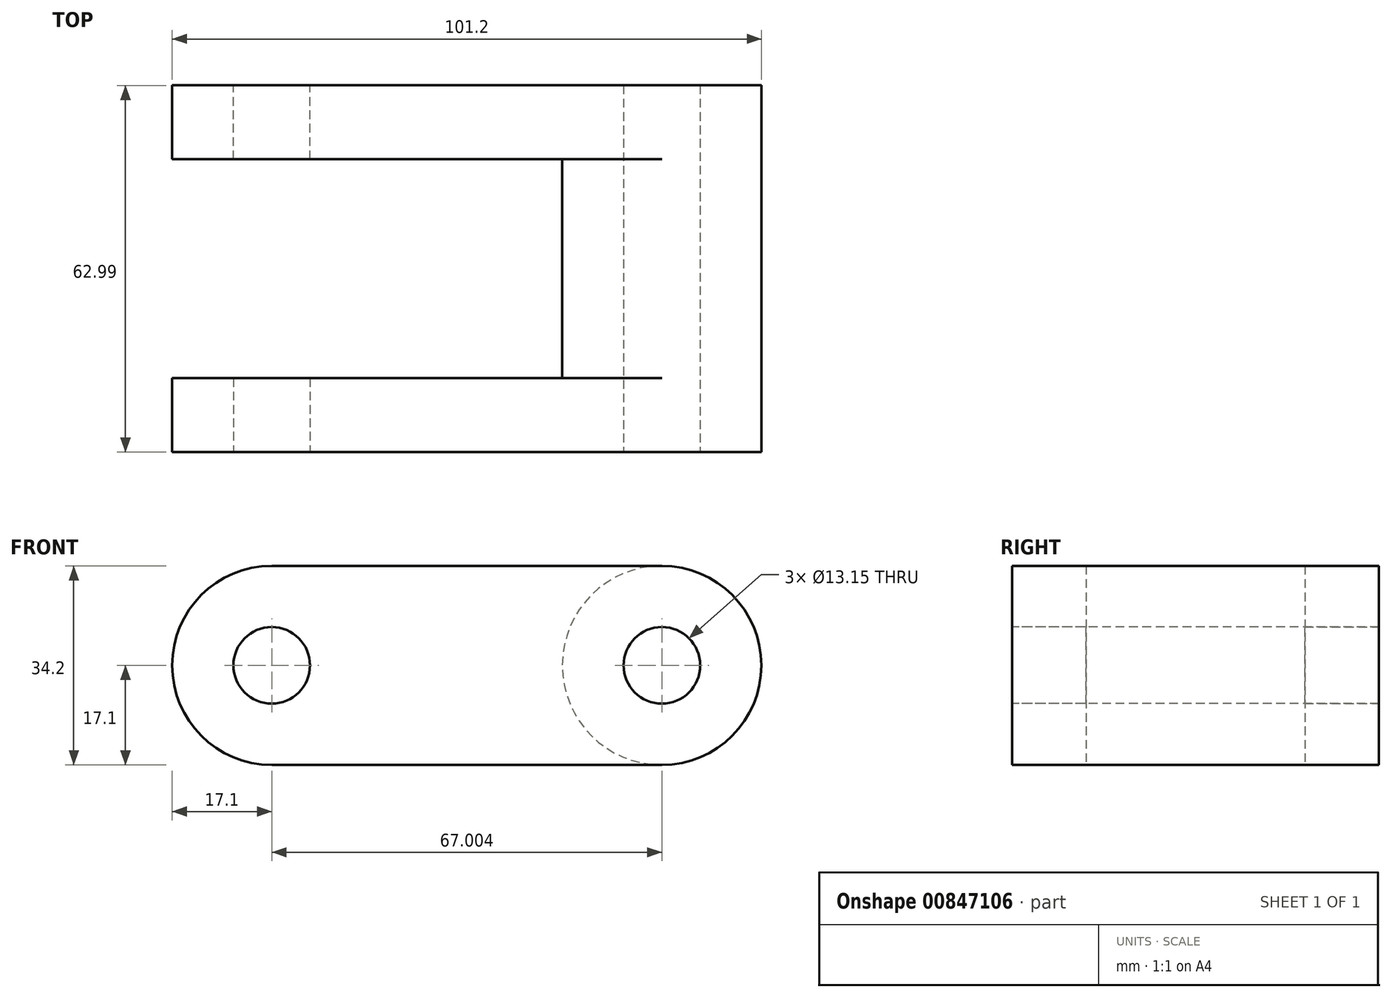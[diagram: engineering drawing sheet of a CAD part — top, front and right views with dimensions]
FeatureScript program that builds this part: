
annotation { "Feature Type Name" : "Feature", "Feature Type Description" : "" }
export const myFeature = defineFeature(function(context is Context, id is Id, definition is map)
    precondition{}
    {
        {
            var Q0;
            Q0=qCreatedBy(makeId("Front.planeOp"),FACE);
            var sketch = newSketch(context, id + "F0", { "sketchPlane" : qUnion([Q0])});
            skLineSegment(sketch, "E0.bottom", {"start": v(29.51, -17.1) * mm, "end": v(-37.49, -17.1) * mm});
            skLineSegment(sketch, "E0.top", {"start": v(29.51, 17.1) * mm, "end": v(-37.49, 17.1) * mm});
            skLineSegment(sketch, "E0.right", {"start": v(-37.49, -17.1) * mm, "end": v(-37.49, 17.1) * mm});
            skPoint(sketch, "E0.middle", {"position": v(-3.99, 0) * mm});
            skArc(sketch, "E1", {"start": v(-37.49, 17.1) * mm, "mid": v(-54.59, 0) * mm, "end": v(-37.49, -17.1) * mm});
            skArc(sketch, "E2", {"start": v(29.51, -17.1) * mm, "mid": v(46.6, 0) * mm, "end": v(29.51, 17.1) * mm});
            skCircle(sketch, "E3", {"center": v(-37.49, 0) * mm, "radius": 6.57 * mm});
            skCircle(sketch, "E4", {"center": v(29.51, 0) * mm, "radius": 6.57 * mm});
            skArc(sketch, "E5", {"start": v(29.51, 17.1) * mm, "mid": v(12.42, 0) * mm, "end": v(29.51, -17.1) * mm});
            skSolve(sketch);
        }
        {
            var Q0;
            {var subQ5=sQuery(id+"F0.wireOp",EDGE,"E0.bottom");Q0=makeQuery(id+"F0.imprint","IMPRINT",FACE,{"disambiguationData":[TD([[makeQuery(id+"F0.imprint","IMPRINT",EDGE,{"derivedFrom":subQ5}),-1.0]])]});}
            var Q1;
            {var subQ0=sQuery(id+"F0.wireOp",EDGE,"E1");Q1=makeQuery(id+"F0.imprint","IMPRINT",FACE,{"disambiguationData":[TD([[makeQuery(id+"F0.imprint","IMPRINT",EDGE,{"derivedFrom":subQ0}),1.0]])]});}
            extrude(context, id + "F1", {"entities" : qUnion([Q0, Q1]), "oppositeDirection" : true, "depth" : 12.7 * mm, "offsetDistance" : 25.4 * mm});
        }
        {
            var Q0;
            Q0=makeQuery(id+"F0.imprint","IMPRINT",FACE,{"disambiguationData":[TD([[makeQuery(id+"F0.imprint","IMPRINT",EDGE,{"derivedFrom":sQuery(id+"F0.wireOp",EDGE,"E2")}),1.0]])]});
            extrude(context, id + "F2", {"entities" : qUnion([Q0]), "operationType" : NewBodyOperationType.ADD, "oppositeDirection" : true, "depth" : 31.5 * mm, "offsetDistance" : 25.4 * mm});
        }
        {
            var Q0;
            Q0=makeQuery(id+"F1.opExtrude","SWEPT_BODY",BODY,{"disambiguationData":[OSD([sQuery(id+"F0.wireOp",EDGE,"E0.bottom"),sQuery(id+"F0.wireOp",EDGE,"E0.top"),sQuery(id+"F0.wireOp",EDGE,"E1"),sQuery(id+"F0.wireOp",EDGE,"E3"),sQuery(id+"F0.wireOp",EDGE,"E5")])]});
            var Q1;
            Q1=makeQuery(id+"F2.opExtrude","CAP_FACE",FACE,{"disambiguationData":[OSD([sQuery(id+"F0.wireOp",EDGE,"E2"),sQuery(id+"F0.wireOp",EDGE,"E4"),sQuery(id+"F0.wireOp",EDGE,"E5")])],"isStart":false});
            mirror(context, id + "F3", {"operationType" : NewBodyOperationType.ADD, "entities" : qUnion([Q0]), "mirrorPlane" : qUnion([Q1])});
        }
    });
